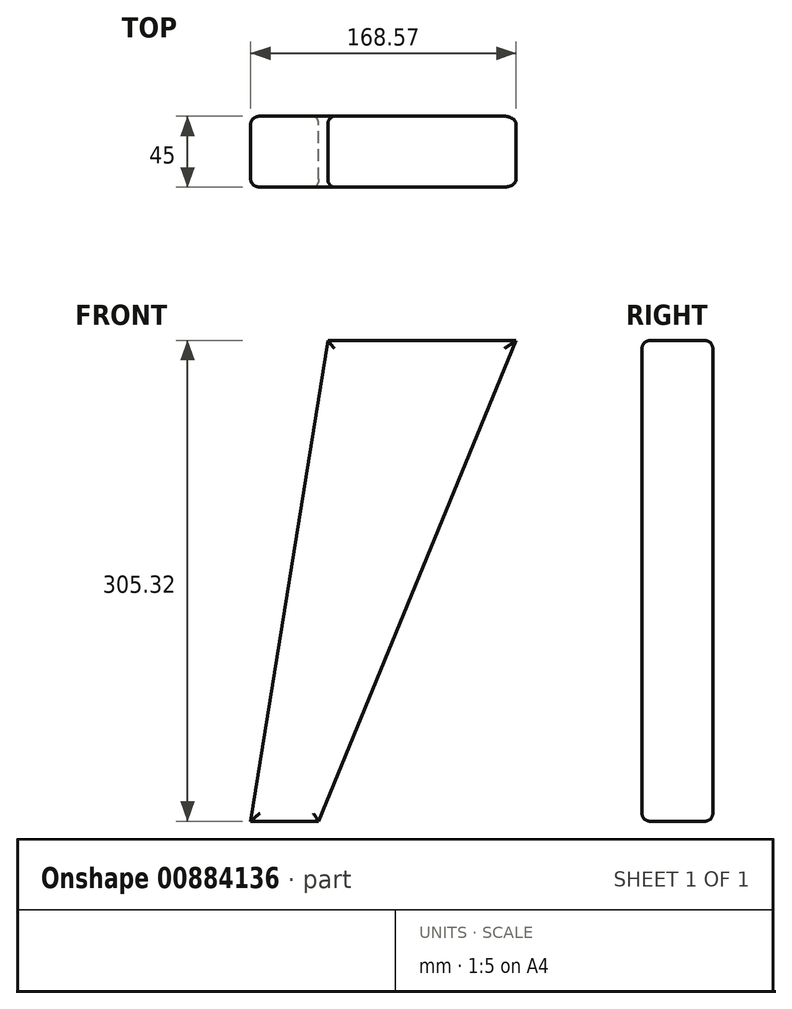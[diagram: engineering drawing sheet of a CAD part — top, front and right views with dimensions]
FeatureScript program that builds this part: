
annotation { "Feature Type Name" : "Feature", "Feature Type Description" : "" }
export const myFeature = defineFeature(function(context is Context, id is Id, definition is map)
    precondition{}
    {
        {
            var Q0;
            Q0=qCreatedBy(makeId("Front.planeOp"),FACE);
            var sketch = newSketch(context, id + "F0", { "sketchPlane" : qUnion([Q0])});
            skPoint(sketch, "E0.middle", {"position": v(1.5, 0) * mm});
            skLineSegment(sketch, "E1", {"start": v(-248.5, -250) * mm, "end": v(-205.28, -250) * mm});
            skLineSegment(sketch, "E2", {"start": v(-205.28, -250) * mm, "end": v(-79.93, 55.32) * mm});
            skLineSegment(sketch, "E3", {"start": v(-199.46, 55.32) * mm, "end": v(-79.93, 55.32) * mm});
            skLineSegment(sketch, "E4", {"start": v(-205.28, -250) * mm, "end": v(-248.5, -250) * mm});
            skLineSegment(sketch, "E5", {"start": v(-199.46, 55.32) * mm, "end": v(-248.5, -250) * mm});
            skSolve(sketch);
        }
        {
            var Q0;
            Q0=makeQuery(id+"F0.imprint","IMPRINT",FACE,{"disambiguationData":[TD([[makeQuery(id+"F0.imprint","IMPRINT",EDGE,{"derivedFrom":sQuery(id+"F0.wireOp",EDGE,"E2")}),1.0]])]});
            extrude(context, id + "F1", {"entities" : qUnion([Q0]), "depth" : 45 * mm, "offsetDistance" : 25 * mm});
        }
        {
            var Q0;
            Q0=makeQuery(id+"F1.opExtrude","CAP_FACE",FACE,{"disambiguationData":[OSD([sQuery(id+"F0.wireOp",EDGE,"E2"),sQuery(id+"F0.wireOp",EDGE,"E3"),sQuery(id+"F0.wireOp",EDGE,"E4"),sQuery(id+"F0.wireOp",EDGE,"E5")])],"isStart":true});
            fillet(context, id + "F2", {"entities" : qUnion([Q0]), "radius" : 5 * mm, "tangentPropagation" : true, "allowEdgeOverflow" : false});
        }
        {
            var Q0;
            Q0=makeQuery(id+"F1.opExtrude","CAP_FACE",FACE,{"disambiguationData":[OSD([sQuery(id+"F0.wireOp",EDGE,"E2"),sQuery(id+"F0.wireOp",EDGE,"E3"),sQuery(id+"F0.wireOp",EDGE,"E4"),sQuery(id+"F0.wireOp",EDGE,"E5")])],"isStart":false});
            fillet(context, id + "F3", {"entities" : qUnion([Q0]), "radius" : 5 * mm, "tangentPropagation" : true, "allowEdgeOverflow" : false});
        }
    });
